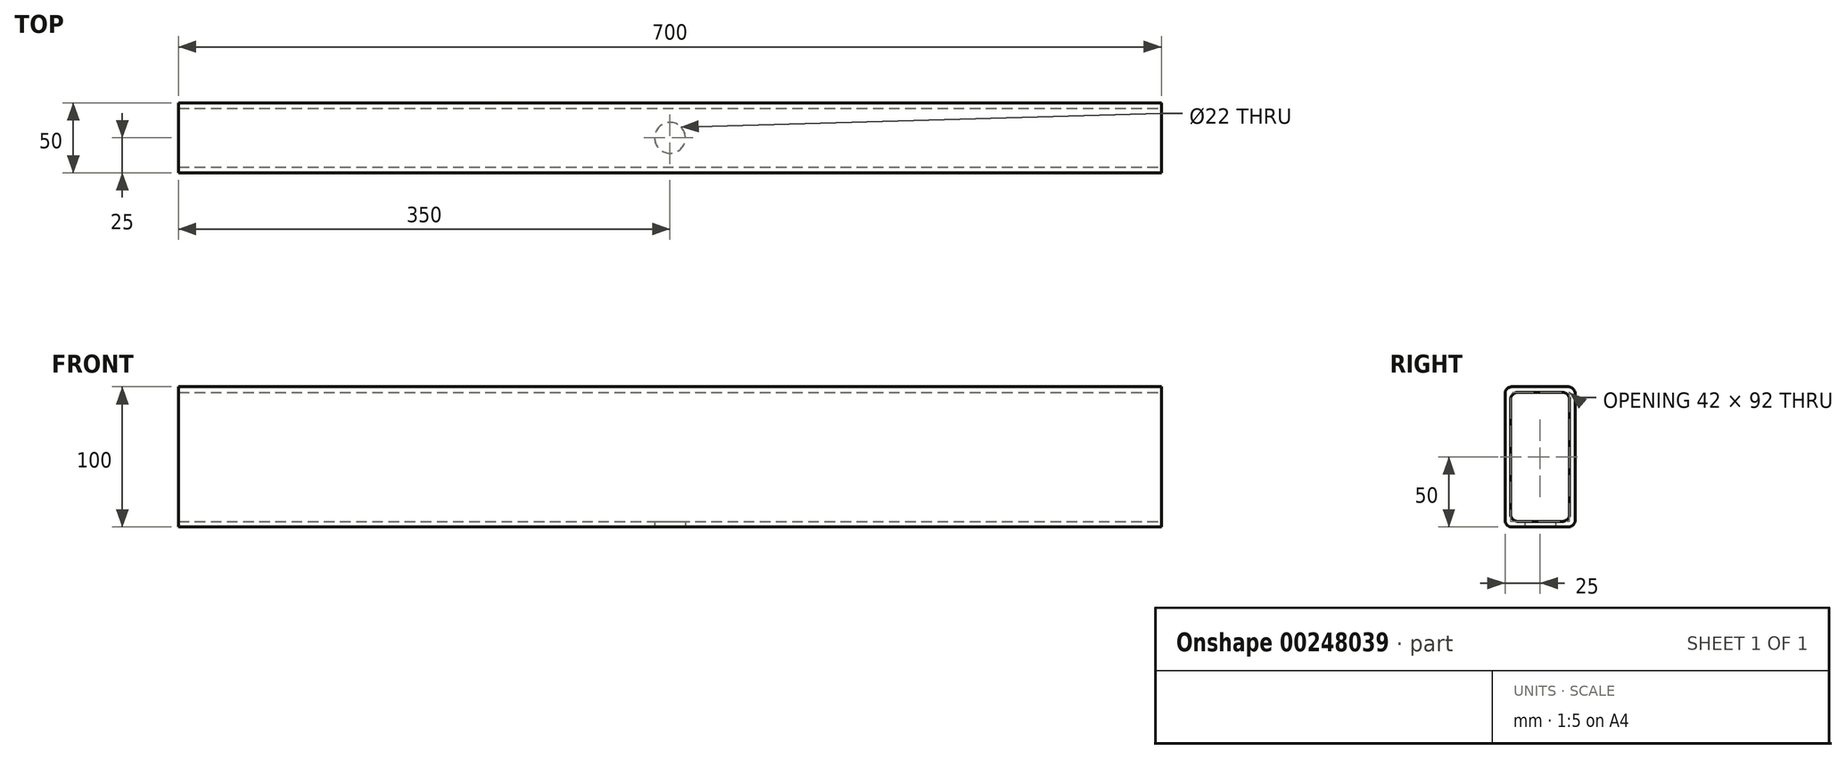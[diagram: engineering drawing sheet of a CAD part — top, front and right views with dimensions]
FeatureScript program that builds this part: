
annotation { "Feature Type Name" : "Feature", "Feature Type Description" : "" }
export const myFeature = defineFeature(function(context is Context, id is Id, definition is map)
    precondition{}
    {
        {
            var Q0;
            Q0=qCreatedBy(makeId("Front.planeOp"),FACE);
            var sketch = newSketch(context, id + "F0", { "sketchPlane" : qUnion([Q0])});
            skLineSegment(sketch, "E0.bottom", {"start": v(-350, -50) * mm, "end": v(350, -50) * mm});
            skLineSegment(sketch, "E0.top", {"start": v(-350, 50) * mm, "end": v(350, 50) * mm});
            skLineSegment(sketch, "E0.left", {"start": v(-350, -50) * mm, "end": v(-350, 50) * mm});
            skLineSegment(sketch, "E0.right", {"start": v(350, -50) * mm, "end": v(350, 50) * mm});
            skPoint(sketch, "E0.middle", {"position": v(0, 0) * mm});
            skSolve(sketch);
        }
        {
            var Q0;
            Q0=makeQuery(id+"F0.imprint","IMPRINT",FACE,{"disambiguationData":[TD([[makeQuery(id+"F0.imprint","IMPRINT",EDGE,{"derivedFrom":sQuery(id+"F0.wireOp",EDGE,"E0.bottom")}),1.0]])]});
            extrude(context, id + "F1", {"entities" : qUnion([Q0]), "depth" : 50 * mm});
        }
        {
            var Q0;
            Q0=makeQuery(id+"F1.opExtrude","SWEPT_FACE",FACE,{"disambiguationData":[OSD([sQuery(id+"F0.wireOp",EDGE,"E0.left")])]});
            var Q1;
            Q1=makeQuery(id+"F1.opExtrude","SWEPT_FACE",FACE,{"disambiguationData":[OSD([sQuery(id+"F0.wireOp",EDGE,"E0.right")])]});
            shell(context, id + "F2", {"entities" : qUnion([Q0, Q1]), "thickness" : 4 * mm});
        }
        {
            var Q0;
            {var subQ0=sQuery(id+"F0.wireOp",EDGE,"E0.top");Q0=makeQuery(id+"F2.opShell","OFFSET_EDGE",EDGE,{"disambiguationData":[OSD([subQ0]),TDD([makeQuery(id+"F1.opExtrude","CAP_EDGE",EDGE,{"disambiguationData":[OSD([subQ0])],"isStart":true})])]});}
            var Q1;
            {var subQ0=sQuery(id+"F0.wireOp",EDGE,"E0.top");Q1=makeQuery(id+"F2.opShell","OFFSET_EDGE",EDGE,{"disambiguationData":[OSD([subQ0]),TDD([makeQuery(id+"F1.opExtrude","CAP_EDGE",EDGE,{"disambiguationData":[OSD([subQ0])],"isStart":false})])]});}
            var Q2;
            Q2=makeQuery(id+"F1.opExtrude","CAP_EDGE",EDGE,{"disambiguationData":[OSD([sQuery(id+"F0.wireOp",EDGE,"E0.top")])],"isStart":true});
            var Q3;
            Q3=makeQuery(id+"F1.opExtrude","CAP_EDGE",EDGE,{"disambiguationData":[OSD([sQuery(id+"F0.wireOp",EDGE,"E0.top")])],"isStart":false});
            var Q4;
            {var subQ0=sQuery(id+"F0.wireOp",EDGE,"E0.bottom");Q4=makeQuery(id+"F2.opShell","OFFSET_EDGE",EDGE,{"disambiguationData":[OSD([subQ0]),TDD([makeQuery(id+"F1.opExtrude","CAP_EDGE",EDGE,{"disambiguationData":[OSD([subQ0])],"isStart":true})])]});}
            var Q5;
            Q5=makeQuery(id+"F1.opExtrude","CAP_EDGE",EDGE,{"disambiguationData":[OSD([sQuery(id+"F0.wireOp",EDGE,"E0.bottom")])],"isStart":false});
            var Q6;
            {var subQ0=sQuery(id+"F0.wireOp",EDGE,"E0.bottom");Q6=makeQuery(id+"F2.opShell","OFFSET_EDGE",EDGE,{"disambiguationData":[OSD([subQ0]),TDD([makeQuery(id+"F1.opExtrude","CAP_EDGE",EDGE,{"disambiguationData":[OSD([subQ0])],"isStart":false})])]});}
            var Q7;
            Q7=makeQuery(id+"F1.opExtrude","CAP_EDGE",EDGE,{"disambiguationData":[OSD([sQuery(id+"F0.wireOp",EDGE,"E0.bottom")])],"isStart":true});
            fillet(context, id + "F3", {"entities" : qUnion([Q0, Q1, Q2, Q3, Q4, Q5, Q6, Q7]), "radius" : 5 * mm, "tangentPropagation" : true, "allowEdgeOverflow" : false});
        }
        {
            var Q0;
            Q0=makeQuery(id+"F1.opExtrude","SWEPT_FACE",FACE,{"disambiguationData":[OSD([sQuery(id+"F0.wireOp",EDGE,"E0.bottom")])]});
            var sketch = newSketch(context, id + "F4", { "sketchPlane" : qUnion([Q0])});
            skPoint(sketch, "E1", {"position": v(0, 25) * mm});
            skSolve(sketch);
        }
        {
            var Q0;
            Q0=sQuery(id+"F4.wireOp",VERTEX,"E1");
            var Q1;
            Q1=makeQuery(id+"F1.opExtrude","SWEPT_BODY",BODY,{"disambiguationData":[OSD([sQuery(id+"F0.wireOp",EDGE,"E0.bottom"),sQuery(id+"F0.wireOp",EDGE,"E0.top"),sQuery(id+"F0.wireOp",EDGE,"E0.left"),sQuery(id+"F0.wireOp",EDGE,"E0.right")])]});
            hole(context, id + "F5", {"style" : HoleStyle.SIMPLE, "endStyle" : HoleEndStyle.BLIND, "holeDiameter" : 22 * mm, "holeDepth" : 4 * mm, "tappedDepth" : 12 * mm, "tapClearance" : 3, "locations" : qUnion([Q0]), "scope" : qUnion([Q1])});
        }
    });
